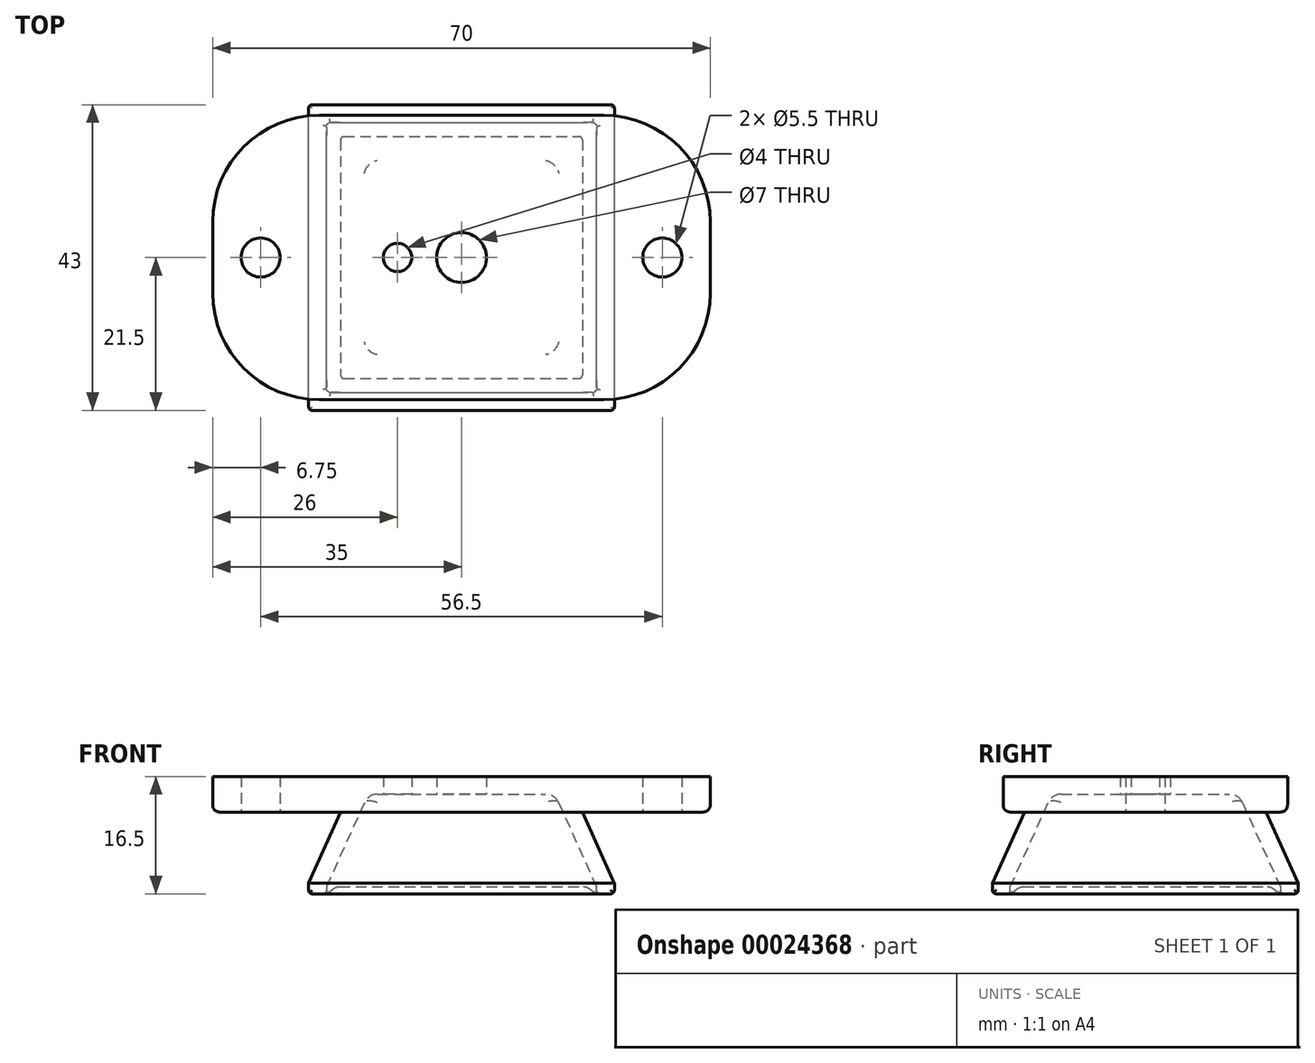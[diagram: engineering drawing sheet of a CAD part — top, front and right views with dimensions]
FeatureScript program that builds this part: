
annotation { "Feature Type Name" : "Feature", "Feature Type Description" : "" }
export const myFeature = defineFeature(function(context is Context, id is Id, definition is map)
    precondition{}
    {
        {
            var Q0;
            Q0=qCreatedBy(makeId("Top.planeOp"),FACE);
            var sketch = newSketch(context, id + "F0", { "sketchPlane" : qUnion([Q0])});
            skLineSegment(sketch, "E0.bottom", {"start": v(-21.5, -21.5) * mm, "end": v(21.5, -21.5) * mm});
            skLineSegment(sketch, "E0.top", {"start": v(-21.5, 21.5) * mm, "end": v(21.5, 21.5) * mm});
            skLineSegment(sketch, "E0.left", {"start": v(-21.5, -21.5) * mm, "end": v(-21.5, 21.5) * mm});
            skLineSegment(sketch, "E0.right", {"start": v(21.5, -21.5) * mm, "end": v(21.5, 21.5) * mm});
            skLineSegment(sketch, "E1", {"start": v(0, 21.5) * mm, "end": v(0, -21.5) * mm, "construction": true});
            skLineSegment(sketch, "E2", {"start": v(-21.5, 0) * mm, "end": v(21.5, 0) * mm, "construction": true});
            skSolve(sketch);
        }
        {
            var Q0;
            Q0=makeQuery(id+"F0.imprint","IMPRINT",FACE,{"disambiguationData":[TD([[makeQuery(id+"F0.imprint","IMPRINT",EDGE,{"derivedFrom":sQuery(id+"F0.wireOp",EDGE,"E0.bottom")}),1.0]])]});
            cPlane(context, id + "F1", {"entities" : qUnion([Q0]), "cplaneType" : CPlaneType.OFFSET, "offset" : 10 * mm, "width" : 150 * mm, "height" : 150 * mm});
        }
        {
            var Q0;
            Q0=qCreatedBy(id+"F1.planeOp",FACE);
            var sketch = newSketch(context, id + "F2", { "sketchPlane" : qUnion([Q0])});
            skLineSegment(sketch, "E3.bottom", {"start": v(-17, 17) * mm, "end": v(17, 17) * mm});
            skLineSegment(sketch, "E3.top", {"start": v(-17, -17) * mm, "end": v(17, -17) * mm});
            skLineSegment(sketch, "E3.left", {"start": v(-17, 17) * mm, "end": v(-17, -17) * mm});
            skLineSegment(sketch, "E3.right", {"start": v(17, 17) * mm, "end": v(17, -17) * mm});
            skLineSegment(sketch, "E4", {"start": v(0, 17) * mm, "end": v(0, -17) * mm, "construction": true});
            skLineSegment(sketch, "E5", {"start": v(-17, 0) * mm, "end": v(17, 0) * mm, "construction": true});
            skSolve(sketch);
        }
        {
            var Q0;
            Q0=makeQuery(id+"F0.imprint","IMPRINT",FACE,{"disambiguationData":[TD([[makeQuery(id+"F0.imprint","IMPRINT",EDGE,{"derivedFrom":sQuery(id+"F0.wireOp",EDGE,"E0.bottom")}),1.0]])]});
            var Q1;
            Q1=makeQuery(id+"F2.imprint","IMPRINT",FACE,{"disambiguationData":[TD([[makeQuery(id+"F2.imprint","IMPRINT",EDGE,{"derivedFrom":sQuery(id+"F2.wireOp",EDGE,"E3.bottom")}),-1.0]])]});
            loft(context, id + "F3", {"sheetProfilesArray" : [{ "sheetProfileEntities" : qUnion([Q0]) }, { "sheetProfileEntities" : qUnion([Q1]) }]});
        }
        {
            var Q0;
            Q0=makeQuery(id+"F3.opLoft","CAP_FACE",FACE,{"disambiguationData":[OSD([makeQuery(id+"F2.imprint","IMPRINT",FACE,{"disambiguationData":[TD([[makeQuery(id+"F2.imprint","IMPRINT",EDGE,{"derivedFrom":sQuery(id+"F2.wireOp",EDGE,"E3.bottom")}),-1.0]])]})])],"isStart":true});
            var sketch = newSketch(context, id + "F4", { "sketchPlane" : qUnion([Q0])});
            skLineSegment(sketch, "E6.bottom", {"start": v(-20, 20) * mm, "end": v(20, 20) * mm});
            skLineSegment(sketch, "E6.top", {"start": v(-20, -20) * mm, "end": v(20, -20) * mm});
            skLineSegment(sketch, "E6.left", {"start": v(-35, 5) * mm, "end": v(-35, -5) * mm});
            skLineSegment(sketch, "E6.right", {"start": v(35, 5) * mm, "end": v(35, -5) * mm});
            skLineSegment(sketch, "E7", {"start": v(0, 20) * mm, "end": v(0, 0) * mm, "construction": true});
            skLineSegment(sketch, "E8", {"start": v(0, 0) * mm, "end": v(35, 0) * mm, "construction": true});
            skCircle(sketch, "E9", {"center": v(-28.25, 0) * mm, "radius": 2.75 * mm});
            skLineSegment(sketch, "E10", {"start": v(-21.5, 0) * mm, "end": v(-35, 0) * mm, "construction": true});
            skCircle(sketch, "E11.MirrorC", {"center": v(28.25, 0) * mm, "radius": 2.75 * mm});
            skPoint(sketch, "E12.visualSharp", {"position": v(-35, -20) * mm});
            skArc(sketch, "E12.filletArc", {"start": v(-35, -5) * mm, "mid": v(-30.6, -15.6) * mm, "end": v(-20, -20) * mm});
            skPoint(sketch, "E13.visualSharp", {"position": v(-35, 20) * mm});
            skArc(sketch, "E13.filletArc", {"start": v(-20, 20) * mm, "mid": v(-30.6, 15.6) * mm, "end": v(-35, 5) * mm});
            skPoint(sketch, "E14.visualSharp", {"position": v(35, -20) * mm});
            skArc(sketch, "E14.filletArc", {"start": v(20, -20) * mm, "mid": v(30.6, -15.6) * mm, "end": v(35, -5) * mm});
            skPoint(sketch, "E15.visualSharp", {"position": v(35, 20) * mm});
            skArc(sketch, "E15.filletArc", {"start": v(35, 5) * mm, "mid": v(30.6, 15.6) * mm, "end": v(20, 20) * mm});
            skSolve(sketch);
        }
        {
            var Q0;
            Q0 = qSketchRegion(id + "F4", true);
            extrude(context, id + "F5", {"entities" : qUnion([Q0]), "operationType" : NewBodyOperationType.ADD, "depth" : 5 * mm});
        }
        {
            var Q0;
            Q0 = qSketchRegion(id + "F0", true);
            extrude(context, id + "F6", {"entities" : qUnion([Q0]), "operationType" : NewBodyOperationType.ADD, "oppositeDirection" : true, "depth" : 1.5 * mm});
        }
        {
            var Q0;
            Q0=makeQuery(id+"F6.opExtrude","CAP_FACE",FACE,{"disambiguationData":[OSD([sQuery(id+"F0.wireOp",EDGE,"E0.bottom"),sQuery(id+"F0.wireOp",EDGE,"E0.top"),sQuery(id+"F0.wireOp",EDGE,"E0.left"),sQuery(id+"F0.wireOp",EDGE,"E0.right")])],"isStart":false});
            shell(context, id + "F7", {"entities" : qUnion([Q0]), "thickness" : 2.5 * mm});
        }
        {
            var Q0;
            Q0=makeQuery(id+"F4.imprint","IMPRINT",FACE,{"disambiguationData":[TD([[makeQuery(id+"F4.imprint","IMPRINT",EDGE,{"derivedFrom":sQuery(id+"F4.wireOp",EDGE,"E6.bottom")}),-1.0]])]});
            var sketch = newSketch(context, id + "F8", { "sketchPlane" : qUnion([Q0])});
            skLineSegment(sketch, "E16", {"start": v(0, 0) * mm, "end": v(-9, 0) * mm, "construction": true});
            skCircle(sketch, "E17", {"center": v(0, 0) * mm, "radius": 3.5 * mm});
            skCircle(sketch, "E18", {"center": v(-9, 0) * mm, "radius": 2 * mm});
            skSolve(sketch);
        }
        {
            var Q0;
            Q0=makeQuery(id+"F7.opShell","OFFSET_EDGE",EDGE,{"disambiguationData":[OSD([sQuery(id+"F0.wireOp",EDGE,"E0.bottom"),sQuery(id+"F0.wireOp",EDGE,"E0.left"),sQuery(id+"F2.wireOp",EDGE,"E3.top"),sQuery(id+"F2.wireOp",EDGE,"E3.left")])]});
            var Q1;
            Q1=makeQuery(id+"F7.opShell","OFFSET_EDGE",EDGE,{"disambiguationData":[OSD([sQuery(id+"F0.wireOp",EDGE,"E0.bottom"),sQuery(id+"F0.wireOp",EDGE,"E0.right"),sQuery(id+"F2.wireOp",EDGE,"E3.top"),sQuery(id+"F2.wireOp",EDGE,"E3.right")])]});
            var Q2;
            Q2=makeQuery(id+"F7.opShell","OFFSET_EDGE",EDGE,{"disambiguationData":[OSD([sQuery(id+"F0.wireOp",EDGE,"E0.top"),sQuery(id+"F0.wireOp",EDGE,"E0.right"),sQuery(id+"F2.wireOp",EDGE,"E3.bottom"),sQuery(id+"F2.wireOp",EDGE,"E3.right")])]});
            var Q3;
            Q3=makeQuery(id+"F7.opShell","OFFSET_EDGE",EDGE,{"disambiguationData":[OSD([sQuery(id+"F0.wireOp",EDGE,"E0.top"),sQuery(id+"F0.wireOp",EDGE,"E0.left"),sQuery(id+"F2.wireOp",EDGE,"E3.bottom"),sQuery(id+"F2.wireOp",EDGE,"E3.left")])]});
            var Q4;
            Q4=makeQuery(id+"F7.opShell","OFFSET_FACE",FACE,{"disambiguationData":[OSD([sQuery(id+"F4.wireOp",EDGE,"E6.bottom"),sQuery(id+"F4.wireOp",EDGE,"E6.top"),sQuery(id+"F4.wireOp",EDGE,"E6.left"),sQuery(id+"F4.wireOp",EDGE,"E6.right"),sQuery(id+"F4.wireOp",EDGE,"E9"),sQuery(id+"F4.wireOp",EDGE,"E11.MirrorC")])]});
            fillet(context, id + "F9", {"entities" : qUnion([Q0, Q1, Q2, Q3, Q4]), "radius" : 2 * mm, "allowEdgeOverflow" : false});
        }
        {
            var Q0;
            Q0=makeQuery(id+"F6.opExtrude","CAP_FACE",FACE,{"disambiguationData":[OSD([sQuery(id+"F0.wireOp",EDGE,"E0.bottom"),sQuery(id+"F0.wireOp",EDGE,"E0.top"),sQuery(id+"F0.wireOp",EDGE,"E0.left"),sQuery(id+"F0.wireOp",EDGE,"E0.right")])],"isStart":false});
            fillet(context, id + "F10", {"entities" : qUnion([Q0]), "radius" : .5 * mm, "tangentPropagation" : true, "allowEdgeOverflow" : false});
        }
        {
            var Q0;
            Q0=makeQuery(id+"F3.opLoft","SWEPT_EDGE",EDGE,{"disambiguationData":[OSD([sQuery(id+"F0.wireOp",EDGE,"E0.bottom"),sQuery(id+"F0.wireOp",EDGE,"E0.left"),sQuery(id+"F2.wireOp",EDGE,"E3.top"),sQuery(id+"F2.wireOp",EDGE,"E3.left")])]});
            var Q1;
            Q1=makeQuery(id+"F3.opLoft","SWEPT_EDGE",EDGE,{"disambiguationData":[OSD([sQuery(id+"F0.wireOp",EDGE,"E0.top"),sQuery(id+"F0.wireOp",EDGE,"E0.left"),sQuery(id+"F2.wireOp",EDGE,"E3.bottom"),sQuery(id+"F2.wireOp",EDGE,"E3.left")])]});
            var Q2;
            Q2=makeQuery(id+"F3.opLoft","SWEPT_EDGE",EDGE,{"disambiguationData":[OSD([sQuery(id+"F0.wireOp",EDGE,"E0.top"),sQuery(id+"F0.wireOp",EDGE,"E0.right"),sQuery(id+"F2.wireOp",EDGE,"E3.bottom"),sQuery(id+"F2.wireOp",EDGE,"E3.right")])]});
            var Q3;
            Q3=makeQuery(id+"F3.opLoft","SWEPT_EDGE",EDGE,{"disambiguationData":[OSD([sQuery(id+"F0.wireOp",EDGE,"E0.bottom"),sQuery(id+"F0.wireOp",EDGE,"E0.right"),sQuery(id+"F2.wireOp",EDGE,"E3.top"),sQuery(id+"F2.wireOp",EDGE,"E3.right")])]});
            var Q4;
            Q4=makeQuery(id+"F6.opExtrude","SWEPT_EDGE",EDGE,{"disambiguationData":[OSD([sQuery(id+"F0.wireOp",EDGE,"E0.bottom"),sQuery(id+"F0.wireOp",EDGE,"E0.left")])]});
            var Q5;
            Q5=makeQuery(id+"F6.opExtrude","SWEPT_EDGE",EDGE,{"disambiguationData":[OSD([sQuery(id+"F0.wireOp",EDGE,"E0.bottom"),sQuery(id+"F0.wireOp",EDGE,"E0.right")])]});
            var Q6;
            Q6=makeQuery(id+"F6.opExtrude","SWEPT_EDGE",EDGE,{"disambiguationData":[OSD([sQuery(id+"F0.wireOp",EDGE,"E0.top"),sQuery(id+"F0.wireOp",EDGE,"E0.right")])]});
            var Q7;
            Q7=makeQuery(id+"F6.opExtrude","SWEPT_EDGE",EDGE,{"disambiguationData":[OSD([sQuery(id+"F0.wireOp",EDGE,"E0.top"),sQuery(id+"F0.wireOp",EDGE,"E0.left")])]});
            fillet(context, id + "F11", {"entities" : qUnion([Q0, Q1, Q2, Q3, Q4, Q5, Q6, Q7]), "radius" : .5 * mm, "allowEdgeOverflow" : false});
        }
        {
            var Q0;
            Q0=makeQuery(id+"F5.opExtrude","CAP_EDGE",EDGE,{"disambiguationData":[OSD([sQuery(id+"F4.wireOp",EDGE,"E6.right")])],"isStart":true});
            var Q1;
            Q1=makeQuery(id+"F5.opExtrude","CAP_EDGE",EDGE,{"disambiguationData":[OSD([sQuery(id+"F4.wireOp",EDGE,"E6.top")])],"isStart":true});
            var Q2;
            Q2=makeQuery(id+"F5.opExtrude","CAP_EDGE",EDGE,{"disambiguationData":[OSD([sQuery(id+"F4.wireOp",EDGE,"E6.bottom")])],"isStart":true});
            var Q3;
            Q3=makeQuery(id+"F5.opExtrude","CAP_EDGE",EDGE,{"disambiguationData":[OSD([sQuery(id+"F4.wireOp",EDGE,"E6.left")])],"isStart":true});
            var Q4;
            Q4=makeQuery(id+"F5.opExtrude","CAP_EDGE",EDGE,{"disambiguationData":[OSD([sQuery(id+"F4.wireOp",EDGE,"E12.filletArc")])],"isStart":true});
            var Q5;
            Q5=makeQuery(id+"F5.opExtrude","CAP_EDGE",EDGE,{"disambiguationData":[OSD([sQuery(id+"F4.wireOp",EDGE,"E14.filletArc")])],"isStart":true});
            var Q6;
            Q6=makeQuery(id+"F5.opExtrude","CAP_EDGE",EDGE,{"disambiguationData":[OSD([sQuery(id+"F4.wireOp",EDGE,"E15.filletArc")])],"isStart":true});
            var Q7;
            Q7=makeQuery(id+"F5.opExtrude","CAP_EDGE",EDGE,{"disambiguationData":[OSD([sQuery(id+"F4.wireOp",EDGE,"E13.filletArc")])],"isStart":true});
            fillet(context, id + "F12", {"entities" : qUnion([Q0, Q1, Q2, Q3, Q4, Q5, Q6, Q7]), "radius" : 1 * mm, "allowEdgeOverflow" : false});
        }
        {
            var Q0;
            Q0 = qSketchRegion(id + "F8", true);
            extrude(context, id + "F13", {"entities" : qUnion([Q0]), "operationType" : NewBodyOperationType.REMOVE, "endBound" : BoundingType.THROUGH_ALL, "depth" : 6 * mm});
        }
    });
